# Revit family: 712-0220-001-DN40
name_source: partatom
category: Pipe Fittings
units: mm (PartAtom-declared; Revit-internal decimal feet)

## family parameters
Always vertical = Yes
Cut with Voids When Loaded = No
Part Type = Elbow
Round Connector Dimension = Use Diameter
Shared = No
Work Plane-Based = No

## types (1)
- DN040_PN10/16
    Angle = 22.50°
    Body_wallthickness = 55 mm  [stored 0.180446 ft]
    DN040_ PN10/16 = Yes
    DN040_PN10/16 = 712-0040-02-201
    Description_ = AVK FLANGED BEND 22.5° W/LOOSE FLANGES
    FOD = 75 mm
    Flange_thickness = 17 mm
    ID(Radius) = 20 mm  [stored 0.0656168 ft]
    L = 94 mm
    L_Ref = 40 mm  [stored 0.131234 ft]
    Nominal Diameter(DN) = 40 mm  [stored 0.131234 ft]
    RF_Thick = 3 mm  [stored 0.00984252 ft]
    Rf_Dia = 42 mm
    URL product pages = https://www.avkvalves.com

note: [stored X ft] marks values corroborated as IEEE doubles in the binary element streams (Revit-internal decimal feet)

## geometry (parser evidence)
native form markers: Sweep x20
no freeform markers — native parametric forms only
